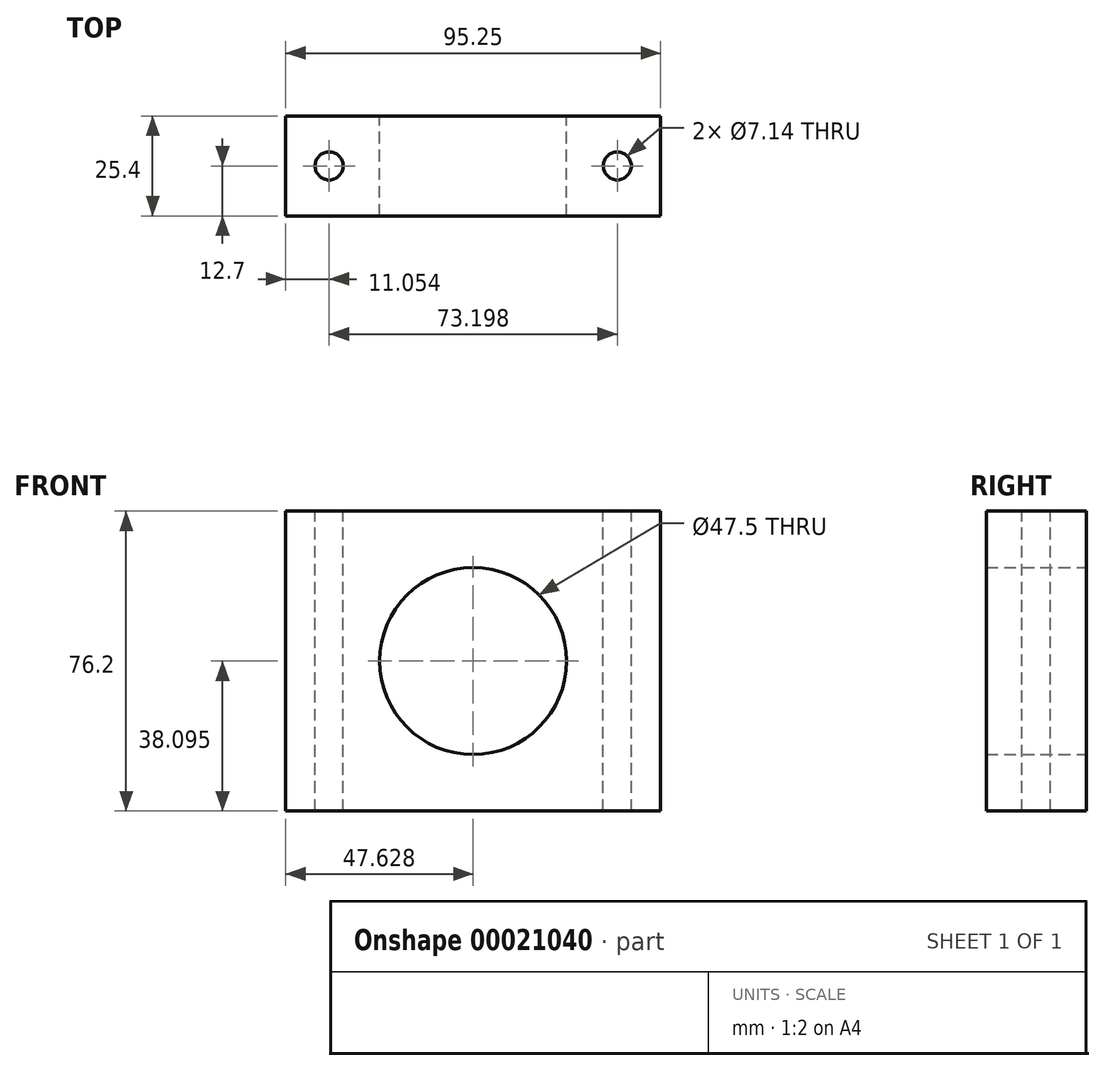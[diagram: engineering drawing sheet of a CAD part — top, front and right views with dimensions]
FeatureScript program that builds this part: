
annotation { "Feature Type Name" : "Feature", "Feature Type Description" : "" }
export const myFeature = defineFeature(function(context is Context, id is Id, definition is map)
    precondition{}
    {
        {
            var Q0;
            Q0=qCreatedBy(makeId("Front.planeOp"),FACE);
            var sketch = newSketch(context, id + "F0", { "sketchPlane" : qUnion([Q0])});
            skLineSegment(sketch, "E0.bottom", {"start": v(-45.02, 30.93) * mm, "end": v(50.23, 30.93) * mm});
            skLineSegment(sketch, "E0.top", {"start": v(-45.02, -45.27) * mm, "end": v(50.23, -45.27) * mm});
            skLineSegment(sketch, "E0.left", {"start": v(-45.02, 30.93) * mm, "end": v(-45.02, -45.27) * mm});
            skLineSegment(sketch, "E0.right", {"start": v(50.23, 30.93) * mm, "end": v(50.23, -45.27) * mm});
            skLineSegment(sketch, "E1", {"start": v(-45.02, -7.17) * mm, "end": v(50.23, -7.17) * mm});
            skCircle(sketch, "E2", {"center": v(2.6, -7.17) * mm, "radius": 23.75 * mm});
            skSolve(sketch);
        }
        {
            var Q0;
            Q0 = qSketchRegion(id + "F0", true);
            extrude(context, id + "F1", {"entities" : qUnion([Q0]), "depth" : 25.4 * mm});
        }
        {
            var Q0;
            Q0=makeQuery(id+"F1.opExtrude","SWEPT_FACE",FACE,{"disambiguationData":[OSD([sQuery(id+"F0.wireOp",EDGE,"E0.bottom")])]});
            var sketch = newSketch(context, id + "F2", { "sketchPlane" : qUnion([Q0])});
            skCircle(sketch, "E3", {"center": v(-33.97, -12.7) * mm, "radius": 3.57 * mm});
            skCircle(sketch, "E4", {"center": v(39.23, -12.7) * mm, "radius": 3.57 * mm});
            skSolve(sketch);
        }
        {
            var Q0;
            Q0=makeQuery(id+"F2.imprint","IMPRINT",FACE,{"disambiguationData":[TD([[makeQuery(id+"F2.imprint","IMPRINT",EDGE,{"derivedFrom":sQuery(id+"F2.wireOp",EDGE,"E4")}),1.0]])]});
            var Q1;
            Q1=makeQuery(id+"F2.imprint","IMPRINT",FACE,{"disambiguationData":[TD([[makeQuery(id+"F2.imprint","IMPRINT",EDGE,{"derivedFrom":sQuery(id+"F2.wireOp",EDGE,"E3")}),1.0]])]});
            extrude(context, id + "F3", {"entities" : qUnion([Q0, Q1]), "operationType" : NewBodyOperationType.REMOVE, "oppositeDirection" : true, "depth" : 76.2 * mm});
        }
    });
